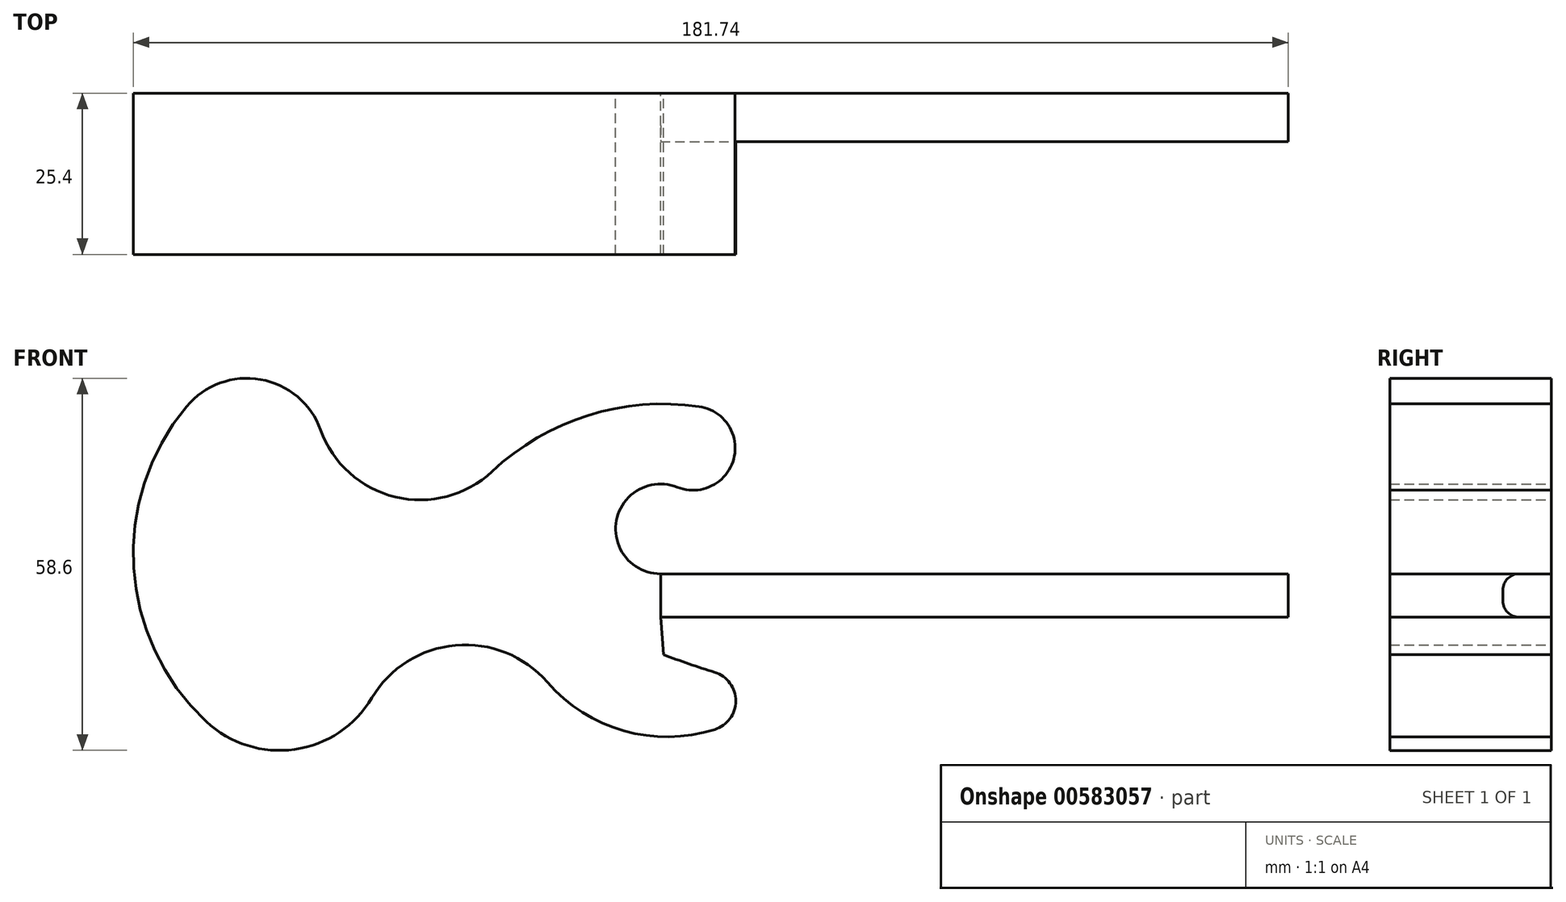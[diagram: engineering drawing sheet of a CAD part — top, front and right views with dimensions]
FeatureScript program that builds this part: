
annotation { "Feature Type Name" : "Feature", "Feature Type Description" : "" }
export const myFeature = defineFeature(function(context is Context, id is Id, definition is map)
    precondition{}
    {
        {
            var Q0;
            Q0=qCreatedBy(makeId("Front.planeOp"),FACE);
            var sketch = newSketch(context, id + "F0", { "sketchPlane" : qUnion([Q0])});
            skLineSegment(sketch, "E0.bottom", {"start": v(0, 10.39) * mm, "end": v(98.77, 10.39) * mm});
            skLineSegment(sketch, "E0.top", {"start": v(0, 3.57) * mm, "end": v(98.77, 3.57) * mm});
            skLineSegment(sketch, "E0.left", {"start": v(0, 10.39) * mm, "end": v(0, 3.57) * mm});
            skLineSegment(sketch, "E0.right", {"start": v(98.77, 10.39) * mm, "end": v(98.77, 3.57) * mm});
            skArc(sketch, "E1", {"start": v(0, 10.39) * mm, "mid": v(-6.95, 18.8) * mm, "end": v(2.64, 24.03) * mm});
            skArc(sketch, "E2", {"start": v(2.64, 24.03) * mm, "mid": v(11.5, 28.47) * mm, "end": v(6.05, 36.75) * mm});
            skArc(sketch, "E3", {"start": v(6.05, 36.75) * mm, "mid": v(-11.4, 35.33) * mm, "end": v(-26.51, 26.51) * mm});
            skArc(sketch, "E4", {"start": v(-26.51, 26.51) * mm, "mid": v(-41.76, 22.5) * mm, "end": v(-53.5, 33.03) * mm});
            skArc(sketch, "E5", {"start": v(-53.5, 33.03) * mm, "mid": v(-62.96, 41) * mm, "end": v(-74.58, 36.75) * mm});
            skArc(sketch, "E6", {"start": v(-74.58, 36.75) * mm, "mid": v(-82.9, 11.32) * mm, "end": v(-71.48, -12.87) * mm});
            skArc(sketch, "E7", {"start": v(-71.48, -12.87) * mm, "mid": v(-57.57, -17.24) * mm, "end": v(-45.43, -9.15) * mm});
            skArc(sketch, "E8", {"start": v(-45.43, -9.15) * mm, "mid": v(-32.27, -0.85) * mm, "end": v(-17.83, -6.67) * mm});
            skArc(sketch, "E9", {"start": v(-17.83, -6.67) * mm, "mid": v(-5.76, -14.33) * mm, "end": v(8.53, -14.11) * mm});
            skArc(sketch, "E10", {"start": v(8.53, -14.11) * mm, "mid": v(11.83, -9.61) * mm, "end": v(8.53, -5.12) * mm});
            skArc(sketch, "E11", {"start": v(8.53, -5.12) * mm, "mid": v(4.46, -3.78) * mm, "end": v(0.44, -2.32) * mm});
            skLineSegment(sketch, "E12.bottom", {"start": v(98.77, 10.39) * mm, "end": v(91.33, 10.39) * mm});
            skLineSegment(sketch, "E13", {"start": v(0.44, -2.32) * mm, "end": v(0, 3.57) * mm});
            skSolve(sketch);
        }
        {
            var Q0;
            Q0=makeQuery(id+"F0.imprint","IMPRINT",FACE,{"disambiguationData":[TD([[makeQuery(id+"F0.imprint","IMPRINT",EDGE,{"derivedFrom":sQuery(id+"F0.wireOp",EDGE,"E0.left")}),-1.0]])]});
            extrude(context, id + "F1", {"entities" : qUnion([Q0]), "depth" : 25.4 * mm, "offsetDistance" : 25.4 * mm});
        }
        {
            var Q0;
            Q0=makeQuery(id+"F0.imprint","IMPRINT",FACE,{"disambiguationData":[TD([[makeQuery(id+"F0.imprint","IMPRINT",EDGE,{"derivedFrom":sQuery(id+"F0.wireOp",EDGE,"E0.bottom")}),-1.0]])]});
            extrude(context, id + "F2", {"entities" : qUnion([Q0]), "operationType" : NewBodyOperationType.ADD, "depth" : 7.62 * mm, "offsetDistance" : 25.4 * mm});
        }
        {
            var Q0;
            Q0=makeQuery(id+"F2.opExtrude","CAP_EDGE",EDGE,{"disambiguationData":[OSD([sQuery(id+"F0.wireOp",EDGE,"E0.top")])],"isStart":false});
            var Q1;
            Q1=makeQuery(id+"F2.opExtrude","CAP_EDGE",EDGE,{"disambiguationData":[OSD([sQuery(id+"F0.wireOp",EDGE,"E0.bottom"),sQuery(id+"F0.wireOp",EDGE,"E12.bottom")])],"isStart":false});
            fillet(context, id + "F3", {"entities" : qUnion([Q0, Q1]), "radius" : 2.54 * mm, "tangentPropagation" : true, "allowEdgeOverflow" : false});
        }
    });
